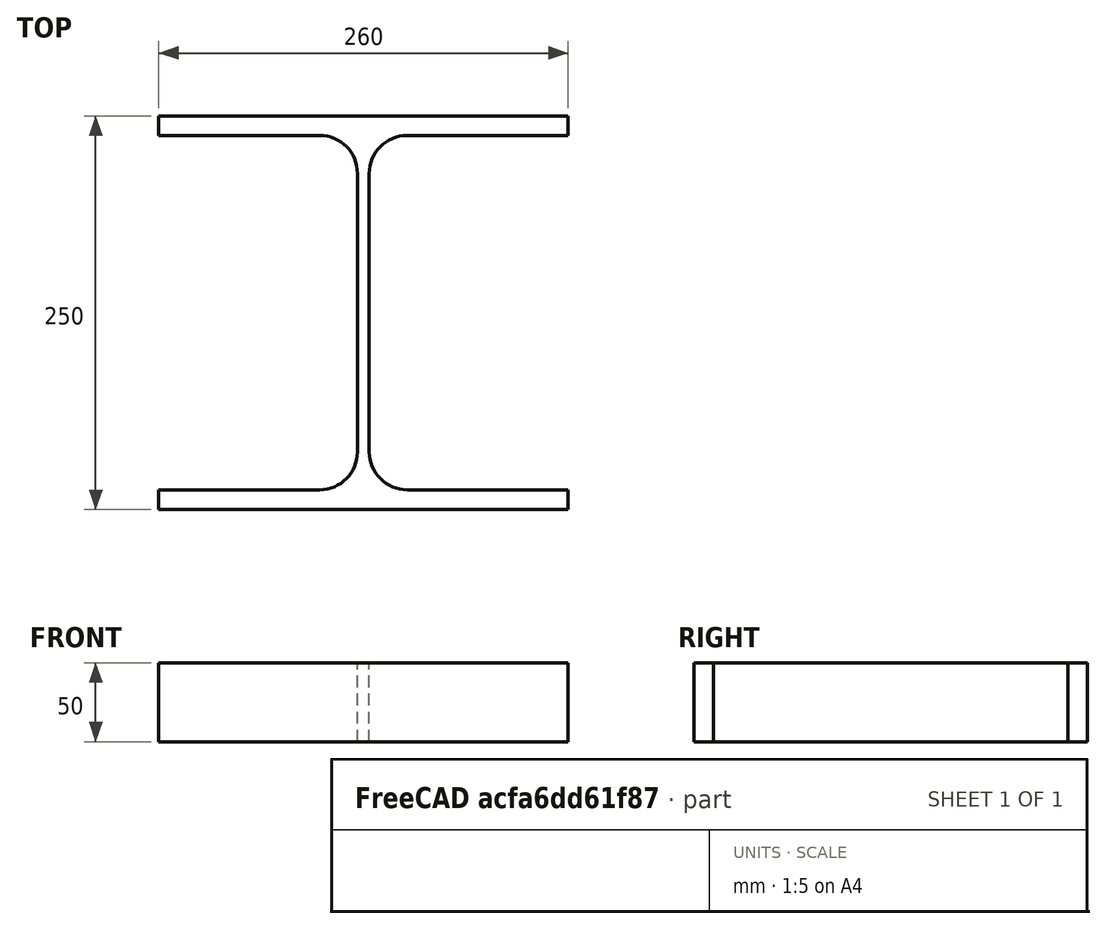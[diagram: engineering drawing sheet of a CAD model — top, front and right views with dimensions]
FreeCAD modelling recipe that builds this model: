
FCSTD DOCUMENT  (FreeCAD 0.15R4671 (Git))
Label: HE-A-Profile 260 DIN1025-3 S235JR
License: All rights reserved
LicenseURL: http://en.wikipedia.org/wiki/All_rights_reserved
objects: Sketcher::SketchObject×1, Part::Extrusion×1
note: 2 computed .brp shape members not serialized (recipe doc carries the construction recipe); baked Part::Feature solids carry a one-line shape summary decoded from their .brp

FEATURE [Sketcher::SketchObject] Sketch
  sketch-geometry (16):
    g0: LineSegment StartX=3.75 StartY=-88.5 StartZ=0 EndX=3.75 EndY=88.5 EndZ=0
    g1: LineSegment StartX=27.75 StartY=112.5 StartZ=0 EndX=130 EndY=112.5 EndZ=0
    g2: LineSegment StartX=130 StartY=112.5 StartZ=0 EndX=130 EndY=125 EndZ=0
    g3: LineSegment StartX=130 StartY=125 StartZ=0 EndX=-130 EndY=125 EndZ=0
    g4: LineSegment StartX=-130 StartY=125 StartZ=0 EndX=-130 EndY=112.5 EndZ=0
    g5: LineSegment StartX=-130 StartY=112.5 StartZ=0 EndX=-27.75 EndY=112.5 EndZ=0
    g6: LineSegment StartX=-3.75 StartY=88.5 StartZ=0 EndX=-3.75 EndY=-88.5 EndZ=0
    g7: LineSegment StartX=-27.75 StartY=-112.5 StartZ=0 EndX=-130 EndY=-112.5 EndZ=0
    g8: LineSegment StartX=-130 StartY=-112.5 StartZ=0 EndX=-130 EndY=-125 EndZ=0
    g9: LineSegment StartX=-130 StartY=-125 StartZ=0 EndX=130 EndY=-125 EndZ=0
    g10: LineSegment StartX=130 StartY=-125 StartZ=0 EndX=130 EndY=-112.5 EndZ=0
    g11: LineSegment StartX=130 StartY=-112.5 StartZ=0 EndX=27.75 EndY=-112.5 EndZ=0
    g12: ArcOfCircle CenterX=27.75 CenterY=88.5 CenterZ=0 NormalX=0 NormalY=0 NormalZ=1 Radius=24 StartAngle=1.5708 EndAngle=3.14159
    g13: ArcOfCircle CenterX=27.75 CenterY=-88.5 CenterZ=0 NormalX=0 NormalY=0 NormalZ=1 Radius=24 StartAngle=3.14159 EndAngle=4.71239
    g14: ArcOfCircle CenterX=-27.75 CenterY=88.5 CenterZ=0 NormalX=0 NormalY=0 NormalZ=1 Radius=24 StartAngle=0 EndAngle=1.5708
    g15: ArcOfCircle CenterX=-27.75 CenterY=-88.5 CenterZ=0 NormalX=0 NormalY=0 NormalZ=1 Radius=24 StartAngle=4.71239 EndAngle=6.28319
  constraints (42):
    c: Vertical(g0)
    c: Coincident(g2,g1)
    c: Vertical(g2)
    c: Coincident(g3,g2)
    c: Coincident(g4,g3)
    c: Vertical(g4)
    c: Coincident(g5,g4)
    c: Horizontal(g5)
    c: Vertical(g6)
    c: Horizontal(g7)
    c: Coincident(g8,g7)
    c: Vertical(g8)
    c: Coincident(g9,g8)
    c: Horizontal(g9)
    c: Coincident(g10,g9)
    c: Vertical(g10)
    c: Coincident(g11,g10)
    c: Horizontal(g11)
    c: Tangent(g1,g12) = 1.5708
    c: Tangent(g0,g12) = 1.5708
    c: Tangent(g0,g13) = 1.5708
    c: Tangent(g11,g13) = 1.5708
    c: Tangent(g5,g14) = 1.5708
    c: Tangent(g6,g14) = 1.5708
    c: Tangent(g6,g15) = 1.5708
    c: Tangent(g7,g15) = 1.5708
    c: Equal(g3,g9)
    c: Equal(g2,g4)
    c: Equal(g4,g8)
    c: Equal(g8,g10)
    c: Equal(g12,g14)
    c: Equal(g14,g15)
    c: Equal(g15,g13)
    c: Symmetric(g2,g3,g-2)
    c: Symmetric(g9,g8,g-2)
    c: Symmetric(g0,g6,g-2)
    c: Symmetric(g2,g9,g-1)
    c: DistanceY(g2,g9) = -250
    c: DistanceX(g3) = -260
    c: DistanceX(g0,g6) = -7.5
    c: DistanceY(g2) = 12.5
    c: Radius(g12) = 24
FEATURE [Part::Extrusion] Extrude  label="HE-A-Profile 260 DIN1025-3 S235JR"
  Base = -> Sketch
  Dir = (0,0,50)
  Solid = true
